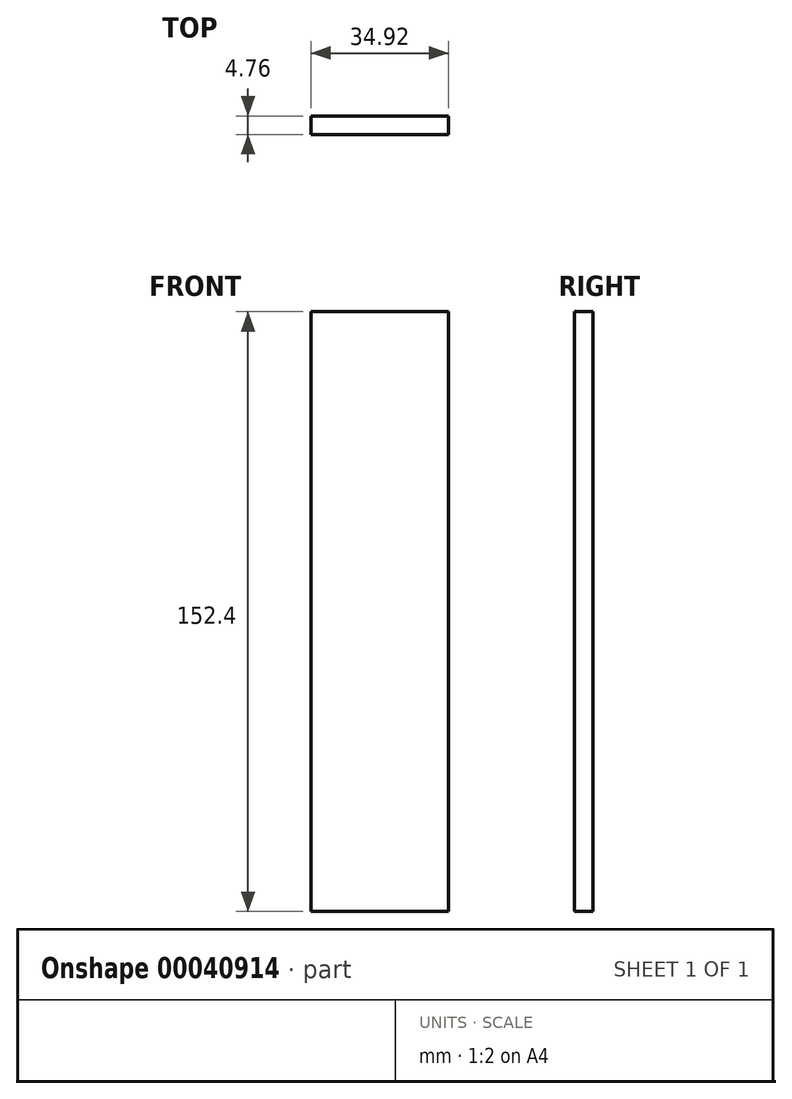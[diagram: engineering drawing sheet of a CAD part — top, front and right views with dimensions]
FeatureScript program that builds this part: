
annotation { "Feature Type Name" : "Feature", "Feature Type Description" : "" }
export const myFeature = defineFeature(function(context is Context, id is Id, definition is map)
    precondition{}
    {
        {
            var Q0;
            Q0=qCreatedBy(makeId("Front.planeOp"),FACE);
            var sketch = newSketch(context, id + "F0", { "sketchPlane" : qUnion([Q0])});
            skLineSegment(sketch, "E0.bottom", {"start": v(-17.46, 152.4) * mm, "end": v(17.46, 152.4) * mm});
            skLineSegment(sketch, "E0.top", {"start": v(-17.46, 0) * mm, "end": v(17.46, 0) * mm});
            skLineSegment(sketch, "E0.left", {"start": v(-17.46, 152.4) * mm, "end": v(-17.46, 0) * mm});
            skLineSegment(sketch, "E0.right", {"start": v(17.46, 152.4) * mm, "end": v(17.46, 0) * mm});
            skPoint(sketch, "E1", {"position": v(0, 0) * mm});
            skSolve(sketch);
        }
        {
            var Q0;
            Q0=makeQuery(id+"F0.imprint","IMPRINT",FACE,{"disambiguationData":[TD([[makeQuery(id+"F0.imprint","IMPRINT",EDGE,{"derivedFrom":sQuery(id+"F0.wireOp",EDGE,"E0.bottom")}),-1.0]])]});
            extrude(context, id + "F1", {"entities" : qUnion([Q0]), "depth" : 4.76 * mm});
        }
    });
